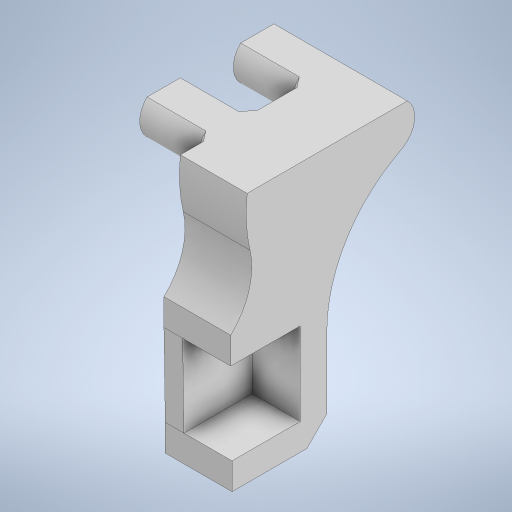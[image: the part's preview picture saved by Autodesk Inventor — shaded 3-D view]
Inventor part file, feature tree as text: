
AUTODESK INVENTOR PART (.ipt)
format: ipt  version: 2024.3 (Build 283343000, 343)  size: 530,432 bytes
history: native  units: mm
features: extrude x10, sketch x8, other x8, reference x7, projected_geometry x6, chamfer x4, plane x1, mirror x1
ambient origin geometry x8: Origin, YZ Plane, XZ Plane, XY Plane, X Axis, Y Axis, Z Axis, Center Point
bodies: Solid1 (feature_tree), Solid2 (feature_tree), Solid3 (feature_tree)
feature tree (45):
  extrude  "Extrusion1"  Depth=0.3mm
  extrude  "Extrusion2"  Depth=1.0mm
  sketch  "Sketch3"  dims[d5=0.3mm d6=1.0mm]
  extrude  "Extrusion3"  Depth=1.0mm
  extrude  "Extrusion4"  Depth=2.0mm
  chamfer  "Chamfer1"  Distance=3.5mm
  extrude  "Extrusion5"  Depth=2.0mm TaperAngle=45.0deg
  extrude  "Extrusion6"  Depth=1.0mm
  chamfer  "Chamfer2"  Distance=15.0mm
  plane  "Work Plane1"
  extrude  "Extrusion7"  Depth=0.5mm
  extrude  "Extrusion8"  Depth=1.4mm
  chamfer  "Chamfer3"  Distance=8.0mm
  extrude  "Extrusion9"  Depth=1.0mm TaperAngle=45.0deg
  chamfer  "Chamfer4"  Distance=0.2mm
  extrude  "Extrusion10"  Depth=0.2mm
  mirror  "Mirror1"
  sketch  "Sketch1"  dims[d0=1.5mm d1=0.0mm d2=0.3mm]
  reference  "Reference1"
  reference  "Reference2"
  sketch  "Sketch2"  dims[d3=1.6mm d4=1.0mm]
  reference  "Reference3"
  reference  "Reference4"
  projected_geometry  "Projected Loop1"
  projected_geometry  "Projected Loop2"
  sketch  "Sketch4"  dims[d7=20.0mm d8=0.0mm d9=2.0mm d10=3.5mm d11=0.0mm]
  reference  "Reference5"
  reference  "Reference6"
  projected_geometry  "Projected Loop3"
  sketch  "Sketch5"  dims[d12=2.0mm d13=0.0mm d14=2.0mm d15=2.0mm d16=45.0deg]
  reference  "Reference7"
  sketch  "Sketch6"  dims[d17=1.0mm d18=1.0mm d19=15.0mm d20=0.0mm]
  sketch  "Sketch7"  dims[d21=0.5mm d22=0.5mm]
  projected_geometry  "Projected Loop6"
  projected_geometry  "Projected Loop7"
  sketch  "Sketch8"  dims[d23=0.5mm d24=0.5mm d25=8.0mm d26=0.0mm d27=1.0mm d28=2.0mm d29=45.0deg d30=0.2mm d31=0.2mm d32=0.2mm d33=5.0mm d34=5.0mm d35=0.0mm d36=0.0mm d37=60.0deg d38=12.0mm d39=5.0mm d40=0.0mm d41=0.6mm d42=2.0mm d43=45.0deg d44=0.2mm d46=2.0mm d47=5.0mm d48=10.0mm d49=5.0mm d50=0.0mm d51=1.5mm d52=2.0mm d53=45.0deg d54=1.4mm d55=0.0mm]
  projected_geometry  "Projected Loop8"
  other  "Pattern of Solid2:1"
  other  "<userpath> TUF\Documents\Inventor\ParkinsonDetection\Prototy-1.iam"
  other  "Prototy-1.iam"
  other  "PCB-V1:1"
  other  "Switch:1"
  other  "Socket:2"
  other  "Socket:1"
  other  "Case-Bottom:1"
